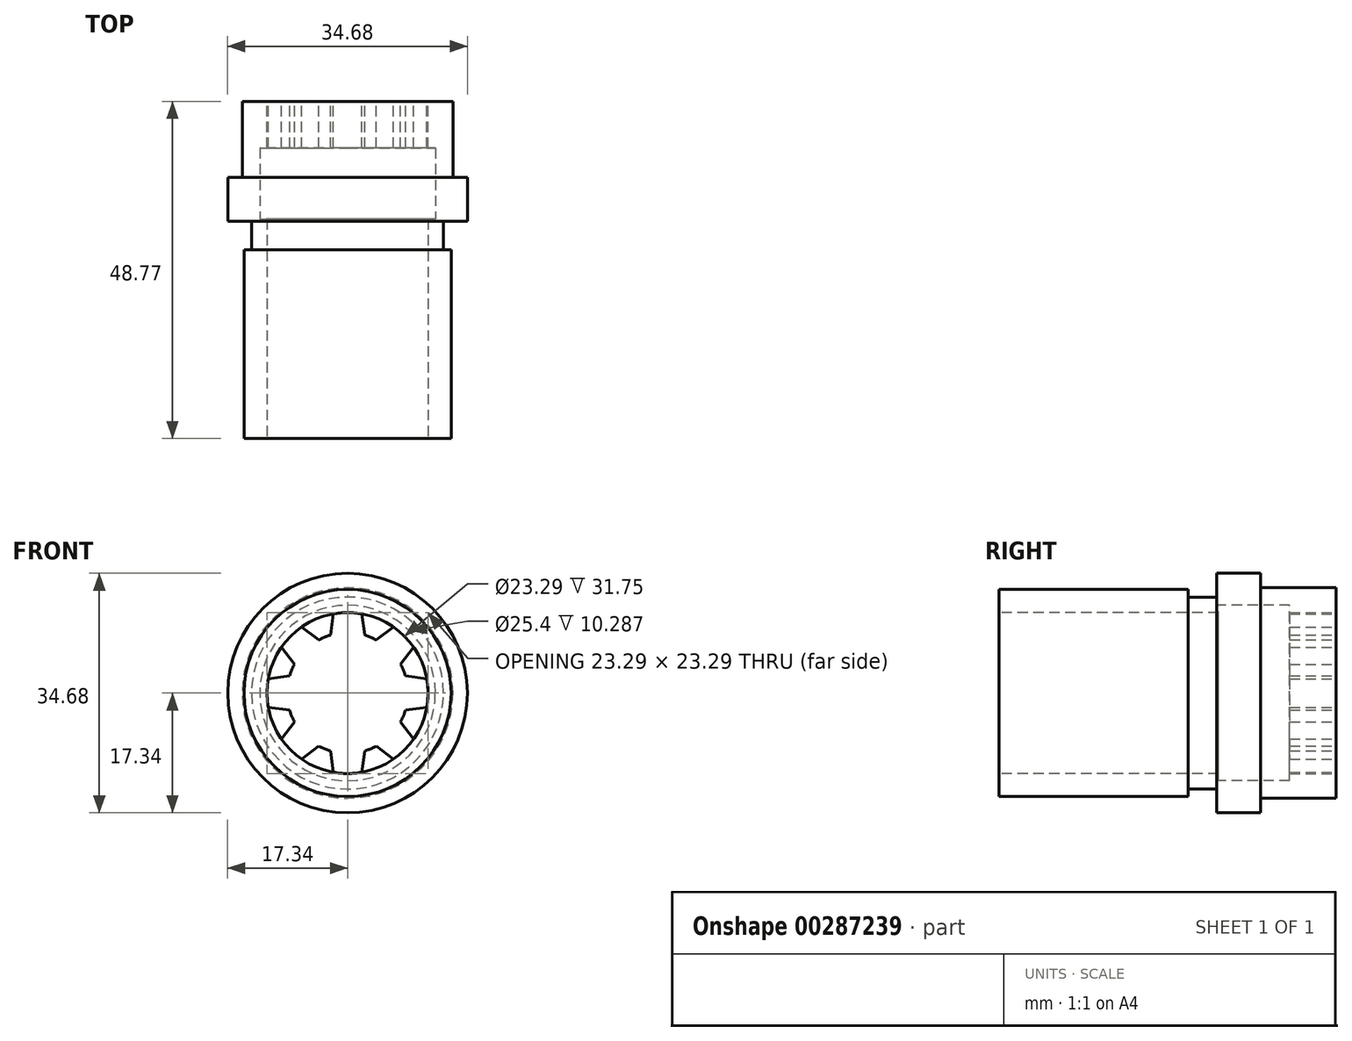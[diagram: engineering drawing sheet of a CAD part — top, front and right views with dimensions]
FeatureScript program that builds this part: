
annotation { "Feature Type Name" : "Feature", "Feature Type Description" : "" }
export const myFeature = defineFeature(function(context is Context, id is Id, definition is map)
    precondition{}
    {
        {
            var Q0;
            Q0=qCreatedBy(makeId("Front.planeOp"),FACE);
            var sketch = newSketch(context, id + "F0", { "sketchPlane" : qUnion([Q0])});
            skCircle(sketch, "E0", {"center": v(0, 0) * mm, "radius": 17.34 * mm});
            skSolve(sketch);
        }
        {
            var Q0;
            Q0=makeQuery(id+"F0.imprint","IMPRINT",FACE,{"disambiguationData":[TD([[makeQuery(id+"F0.imprint","IMPRINT",EDGE,{"derivedFrom":sQuery(id+"F0.wireOp",EDGE,"E0")}),1.0]])]});
            extrude(context, id + "F1", {"entities" : qUnion([Q0]), "oppositeDirection" : true, "depth" : 6.35 * mm});
        }
        {
            var Q0;
            Q0=makeQuery(id+"F1.opExtrude","CAP_FACE",FACE,{"disambiguationData":[OSD([sQuery(id+"F0.wireOp",EDGE,"E0")])],"isStart":true});
            var sketch = newSketch(context, id + "F2", { "sketchPlane" : qUnion([Q0])});
            skCircle(sketch, "E1", {"center": v(0, 0) * mm, "radius": 14.99 * mm});
            skSolve(sketch);
        }
        {
            var Q0;
            Q0 = qSketchRegion(id + "F2", true);
            extrude(context, id + "F3", {"entities" : qUnion([Q0]), "operationType" : NewBodyOperationType.ADD, "depth" : 31.45 * mm});
        }
        {
            var Q0;
            Q0=makeQuery(id+"F1.opExtrude","CAP_FACE",FACE,{"disambiguationData":[OSD([sQuery(id+"F0.wireOp",EDGE,"E0")])],"isStart":false});
            var sketch = newSketch(context, id + "F4", { "sketchPlane" : qUnion([Q0])});
            skCircle(sketch, "E2", {"center": v(0, 0) * mm, "radius": 15.24 * mm});
            skSolve(sketch);
        }
        {
            var Q0;
            Q0 = qSketchRegion(id + "F4", true);
            extrude(context, id + "F5", {"entities" : qUnion([Q0]), "operationType" : NewBodyOperationType.ADD, "depth" : 10.97 * mm});
        }
        {
            var Q0;
            Q0=qCreatedBy(makeId("Right.planeOp"),FACE);
            var sketch = newSketch(context, id + "F6", { "sketchPlane" : qUnion([Q0])});
            skLineSegment(sketch, "E3", {"start": v(-4.11, 14.99) * mm, "end": v(-4.11, 13.89) * mm});
            skLineSegment(sketch, "E4", {"start": v(-4.11, 13.89) * mm, "end": v(0, 13.89) * mm});
            skLineSegment(sketch, "E5", {"start": v(-43.32, 0) * mm, "end": v(42.88, 0) * mm, "construction": true});
            skLineSegment(sketch, "E6", {"start": v(6.35, -17.34) * mm, "end": v(0, -17.34) * mm});
            skLineSegment(sketch, "E7", {"start": v(0, 17.34) * mm, "end": v(6.35, 17.34) * mm});
            skLineSegment(sketch, "E8", {"start": v(-31.45, 14.99) * mm, "end": v(0, 14.99) * mm});
            skLineSegment(sketch, "E9", {"start": v(0, 14.99) * mm, "end": v(0, 13.89) * mm});
            skLineSegment(sketch, "E10", {"start": v(0, 14.99) * mm, "end": v(-4.11, 14.99) * mm});
            skSolve(sketch);
        }
        {
            var Q0;
            Q0 = qSketchRegion(id + "F6", true);
            var Q1;
            Q1=sQuery(id+"F6.wireOp",EDGE,"E5");
            revolve(context, id + "F7", {"operationType" : NewBodyOperationType.REMOVE, "entities" : qUnion([Q0]), "axis" : qUnion([Q1]), "revolveType" : RevolveType.FULL, "oppositeDirection" : true});
        }
        {
            var Q0;
            Q0=makeQuery(id+"F3.opExtrude","CAP_FACE",FACE,{"disambiguationData":[OSD([sQuery(id+"F2.wireOp",EDGE,"E1")])],"isStart":false});
            var sketch = newSketch(context, id + "F8", { "sketchPlane" : qUnion([Q0])});
            skCircle(sketch, "E11", {"center": v(0, 0) * mm, "radius": 11.65 * mm});
            skSolve(sketch);
        }
        {
            var Q0;
            Q0=makeQuery(id+"F8.imprint","IMPRINT",FACE,{"disambiguationData":[TD([[makeQuery(id+"F8.imprint","IMPRINT",EDGE,{"derivedFrom":sQuery(id+"F8.wireOp",EDGE,"E11")}),1.0]])]});
            extrude(context, id + "F9", {"entities" : qUnion([Q0]), "operationType" : NewBodyOperationType.REMOVE, "oppositeDirection" : true, "depth" : 31.75 * mm});
        }
        {
            var Q0;
            Q0=makeQuery(id+"F9.boolean.opBoolean","COPY",FACE,{"derivedFrom":makeQuery(id+"F9.opExtrude","CAP_FACE",FACE,{"disambiguationData":[OSD([sQuery(id+"F8.wireOp",EDGE,"E11")])],"isStart":false})});
            var sketch = newSketch(context, id + "F10", { "sketchPlane" : qUnion([Q0])});
            skCircle(sketch, "E12", {"center": v(0, 0) * mm, "radius": 12.7 * mm});
            skSolve(sketch);
        }
        {
            var Q0;
            Q0 = qSketchRegion(id + "F10", true);
            extrude(context, id + "F11", {"entities" : qUnion([Q0]), "operationType" : NewBodyOperationType.REMOVE, "oppositeDirection" : true, "depth" : 10.29 * mm});
        }
        {
            var Q0;
            Q0=makeQuery(id+"F5.opExtrude","CAP_FACE",FACE,{"disambiguationData":[OSD([sQuery(id+"F4.wireOp",EDGE,"E2")])],"isStart":false});
            var sketch = newSketch(context, id + "F12", { "sketchPlane" : qUnion([Q0])});
            skArc(sketch, "E13", {"start": v(-6.65, 9.56) * mm, "mid": v(-8.23, 8.23) * mm, "end": v(-9.56, 6.65) * mm});
            skArc(sketch, "E14", {"start": v(-7.68, 4.17) * mm, "mid": v(-8.07, 3.34) * mm, "end": v(-8.38, 2.48) * mm});
            skLineSegment(sketch, "E15", {"start": v(0, 11.65) * mm, "end": v(0, 4.66) * mm, "construction": true});
            skLineSegment(sketch, "E16", {"start": v(-2.06, 11.46) * mm, "end": v(-2.48, 8.38) * mm});
            skLineSegment(sketch, "E17", {"start": v(2.06, 11.46) * mm, "end": v(2.48, 8.38) * mm});
            skLineSegment(sketch, "E18.1.0", {"start": v(-6.65, 9.56) * mm, "end": v(-4.17, 7.68) * mm});
            skLineSegment(sketch, "E18.1.1", {"start": v(-9.56, 6.65) * mm, "end": v(-7.68, 4.17) * mm});
            skLineSegment(sketch, "E18.2.0", {"start": v(-11.46, 2.06) * mm, "end": v(-8.38, 2.48) * mm});
            skLineSegment(sketch, "E18.2.1", {"start": v(-11.46, -2.06) * mm, "end": v(-8.38, -2.48) * mm});
            skLineSegment(sketch, "E18.3.0", {"start": v(-9.56, -6.65) * mm, "end": v(-7.68, -4.17) * mm});
            skLineSegment(sketch, "E18.3.1", {"start": v(-6.65, -9.56) * mm, "end": v(-4.17, -7.68) * mm});
            skLineSegment(sketch, "E18.4.0", {"start": v(-2.06, -11.46) * mm, "end": v(-2.48, -8.38) * mm});
            skLineSegment(sketch, "E18.4.1", {"start": v(2.06, -11.46) * mm, "end": v(2.48, -8.38) * mm});
            skLineSegment(sketch, "E18.5.0", {"start": v(6.65, -9.56) * mm, "end": v(4.17, -7.68) * mm});
            skLineSegment(sketch, "E18.5.1", {"start": v(9.56, -6.65) * mm, "end": v(7.68, -4.17) * mm});
            skLineSegment(sketch, "E18.6.0", {"start": v(11.46, -2.06) * mm, "end": v(8.38, -2.48) * mm});
            skLineSegment(sketch, "E18.6.1", {"start": v(11.46, 2.06) * mm, "end": v(8.38, 2.48) * mm});
            skLineSegment(sketch, "E18.7.0", {"start": v(9.56, 6.65) * mm, "end": v(7.68, 4.17) * mm});
            skLineSegment(sketch, "E18.7.1", {"start": v(6.65, 9.56) * mm, "end": v(4.17, 7.68) * mm});
            skArc(sketch, "E19.trimOffspring", {"start": v(-11.46, 2.06) * mm, "mid": v(-11.65, 0) * mm, "end": v(-11.46, -2.06) * mm});
            skArc(sketch, "E20.trimOffspring", {"start": v(-8.38, -2.48) * mm, "mid": v(-8.07, -3.34) * mm, "end": v(-7.68, -4.17) * mm});
            skArc(sketch, "E21.trimOffspring", {"start": v(-9.56, -6.65) * mm, "mid": v(-8.23, -8.23) * mm, "end": v(-6.65, -9.56) * mm});
            skArc(sketch, "E22.trimOffspring", {"start": v(-4.17, -7.68) * mm, "mid": v(-3.34, -8.07) * mm, "end": v(-2.48, -8.38) * mm});
            skArc(sketch, "E23.trimOffspring", {"start": v(-2.06, -11.46) * mm, "mid": v(0, -11.65) * mm, "end": v(2.06, -11.46) * mm});
            skArc(sketch, "E24.trimOffspring", {"start": v(2.48, -8.38) * mm, "mid": v(3.34, -8.07) * mm, "end": v(4.17, -7.68) * mm});
            skArc(sketch, "E25.trimOffspring", {"start": v(6.65, -9.56) * mm, "mid": v(8.23, -8.23) * mm, "end": v(9.56, -6.65) * mm});
            skArc(sketch, "E26.trimOffspring", {"start": v(7.68, -4.17) * mm, "mid": v(8.07, -3.34) * mm, "end": v(8.38, -2.48) * mm});
            skArc(sketch, "E27.trimOffspring", {"start": v(11.46, -2.06) * mm, "mid": v(11.65, 0) * mm, "end": v(11.46, 2.06) * mm});
            skArc(sketch, "E28.trimOffspring", {"start": v(8.38, 2.48) * mm, "mid": v(8.07, 3.34) * mm, "end": v(7.68, 4.17) * mm});
            skArc(sketch, "E29.trimOffspring", {"start": v(9.56, 6.65) * mm, "mid": v(8.23, 8.23) * mm, "end": v(6.65, 9.56) * mm});
            skArc(sketch, "E30.trimOffspring", {"start": v(2.06, 11.46) * mm, "mid": v(0, 11.65) * mm, "end": v(-2.06, 11.46) * mm});
            skArc(sketch, "E31.trimOffspring", {"start": v(4.17, 7.68) * mm, "mid": v(3.34, 8.07) * mm, "end": v(2.48, 8.38) * mm});
            skArc(sketch, "E32.trimOffspring", {"start": v(-2.48, 8.38) * mm, "mid": v(-3.34, 8.07) * mm, "end": v(-4.17, 7.68) * mm});
            skSolve(sketch);
        }
        {
            var Q0;
            Q0 = qSketchRegion(id + "F12", true);
            var Q1;
            Q1=makeQuery(id+"F11.boolean.opBoolean","COPY",FACE,{"derivedFrom":makeQuery(id+"F11.opExtrude","CAP_FACE",FACE,{"disambiguationData":[OSD([sQuery(id+"F10.wireOp",EDGE,"E12")])],"isStart":false})});
            extrude(context, id + "F13", {"entities" : qUnion([Q0]), "operationType" : NewBodyOperationType.REMOVE, "endBound" : BoundingType.UP_TO_SURFACE, "oppositeDirection" : true, "endBoundEntityFace" : qUnion([Q1]), "depth" : 25.4 * mm});
        }
    });
